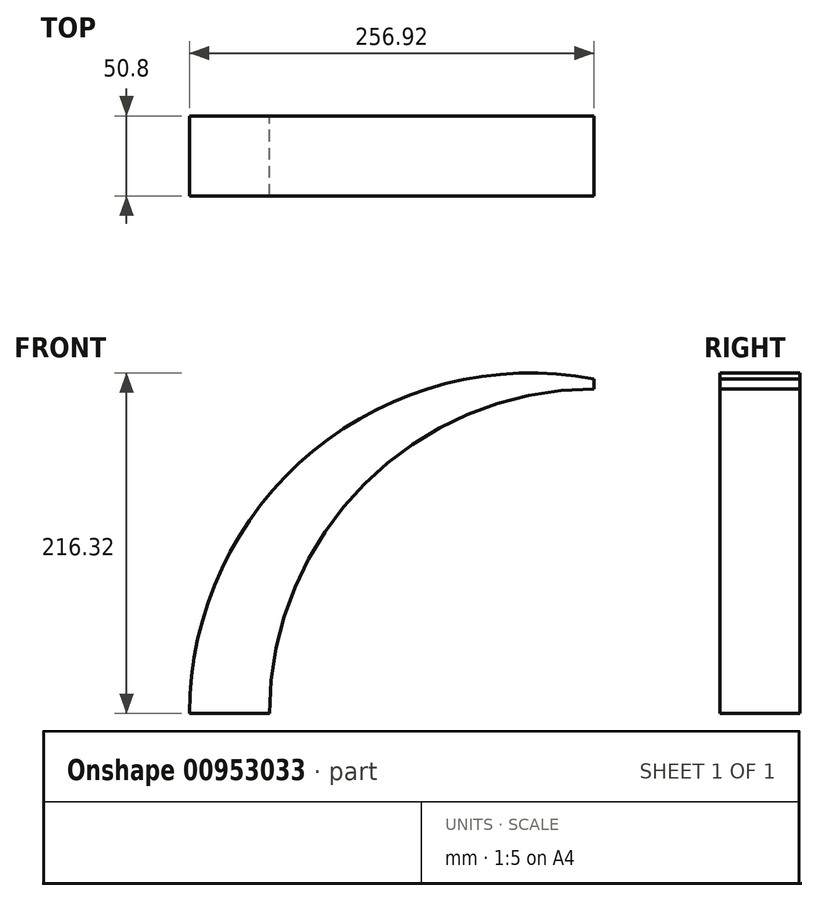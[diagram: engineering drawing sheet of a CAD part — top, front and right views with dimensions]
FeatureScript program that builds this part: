
annotation { "Feature Type Name" : "Feature", "Feature Type Description" : "" }
export const myFeature = defineFeature(function(context is Context, id is Id, definition is map)
    precondition{}
    {
        {
            var Q0;
            Q0=qCreatedBy(makeId("Front.planeOp"),FACE);
            var sketch = newSketch(context, id + "F0", { "sketchPlane" : qUnion([Q0])});
            skArc(sketch, "E0", {"start": v(0, 206.12) * mm, "mid": v(-145.75, 145.75) * mm, "end": v(-206.12, 0) * mm});
            skPoint(sketch, "E1", {"position": v(0, 206.12) * mm});
            skPoint(sketch, "E2", {"position": v(-206.12, 0) * mm});
            skLineSegment(sketch, "E3", {"start": v(0, 206.12) * mm, "end": v(0, 212.47) * mm});
            skLineSegment(sketch, "E4", {"start": v(-206.12, 0) * mm, "end": v(-256.92, 0) * mm});
            skArc(sketch, "E5", {"start": v(0, 212.47) * mm, "mid": v(-178.46, 166.7) * mm, "end": v(-256.92, 0) * mm});
            skLineSegment(sketch, "E6.bottom", {"start": v(-256.92, 0) * mm, "end": v(-250.57, 0) * mm});
            skLineSegment(sketch, "E6.top", {"start": v(-256.92, -76.2) * mm, "end": v(-250.57, -76.2) * mm});
            skLineSegment(sketch, "E6.left", {"start": v(-256.92, 0) * mm, "end": v(-256.92, -76.2) * mm});
            skLineSegment(sketch, "E6.right", {"start": v(-250.57, 0) * mm, "end": v(-250.57, -76.2) * mm});
            skPoint(sketch, "E7", {"position": v(-231.52, 0) * mm});
            skLineSegment(sketch, "E8", {"start": v(-231.52, 0) * mm, "end": v(-231.52, -99.24) * mm, "construction": true});
            skSolve(sketch);
        }
        {
            var Q0;
            Q0=makeQuery(id+"F0.imprint","IMPRINT",FACE,{"disambiguationData":[TD([[makeQuery(id+"F0.imprint","IMPRINT",EDGE,{"derivedFrom":sQuery(id+"F0.wireOp",EDGE,"E0")}),-1.0]])]});
            extrude(context, id + "F1", {"entities" : qUnion([Q0]), "depth" : 25.4 * mm, "offsetDistance" : 25.4 * mm, "hasSecondDirection" : true, "secondDirectionOppositeDirection" : true, "secondDirectionDepth" : 25.4 * mm});
        }
    });
